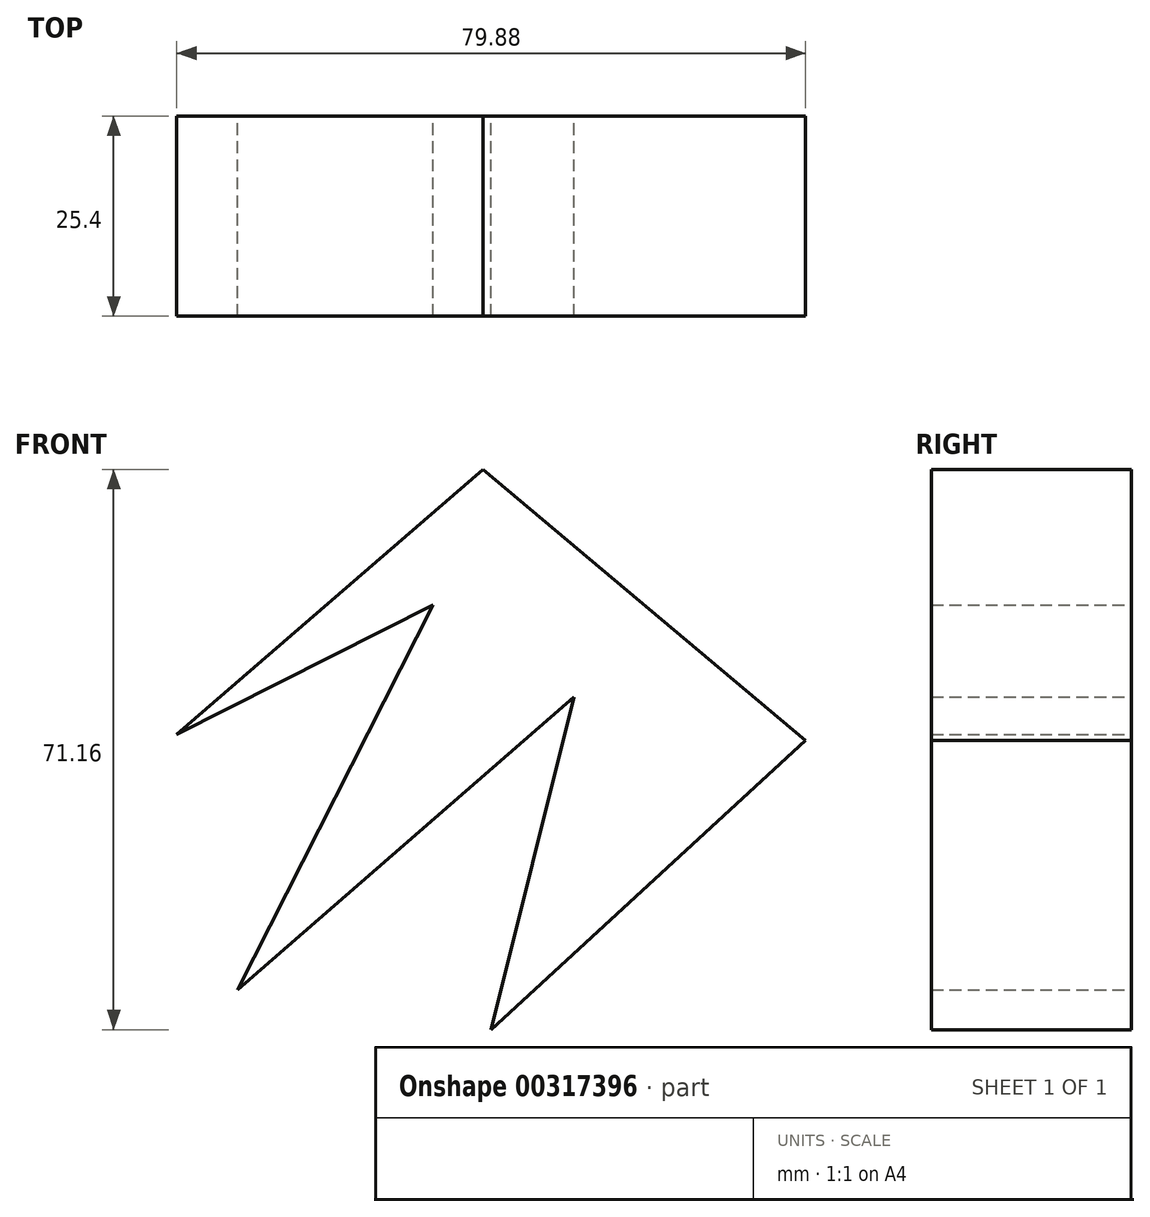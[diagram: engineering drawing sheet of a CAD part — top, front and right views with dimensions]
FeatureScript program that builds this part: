
annotation { "Feature Type Name" : "Feature", "Feature Type Description" : "" }
export const myFeature = defineFeature(function(context is Context, id is Id, definition is map)
    precondition{}
    {
        {
            var Q0;
            Q0=qCreatedBy(makeId("Front.planeOp"),FACE);
            var sketch = newSketch(context, id + "F0", { "sketchPlane" : qUnion([Q0])});
            skLineSegment(sketch, "E0", {"start": v(-24.35, 4) * mm, "end": v(14.54, 37.65) * mm});
            skLineSegment(sketch, "E1", {"start": v(14.54, 37.65) * mm, "end": v(55.53, 3.24) * mm});
            skLineSegment(sketch, "E2", {"start": v(55.53, 3.24) * mm, "end": v(15.59, -33.51) * mm});
            skLineSegment(sketch, "E3", {"start": v(15.59, -33.51) * mm, "end": v(26.1, 8.76) * mm});
            skLineSegment(sketch, "E4", {"start": v(26.1, 8.76) * mm, "end": v(-16.64, -28.45) * mm});
            skLineSegment(sketch, "E5", {"start": v(-16.64, -28.45) * mm, "end": v(8.23, 20.42) * mm});
            skLineSegment(sketch, "E6", {"start": v(8.23, 20.42) * mm, "end": v(-24.35, 4) * mm});
            skSolve(sketch);
        }
        {
            var Q0;
            Q0 = qSketchRegion(id + "F0", true);
            extrude(context, id + "F1", {"entities" : qUnion([Q0]), "depth" : 25.4 * mm});
        }
    });
